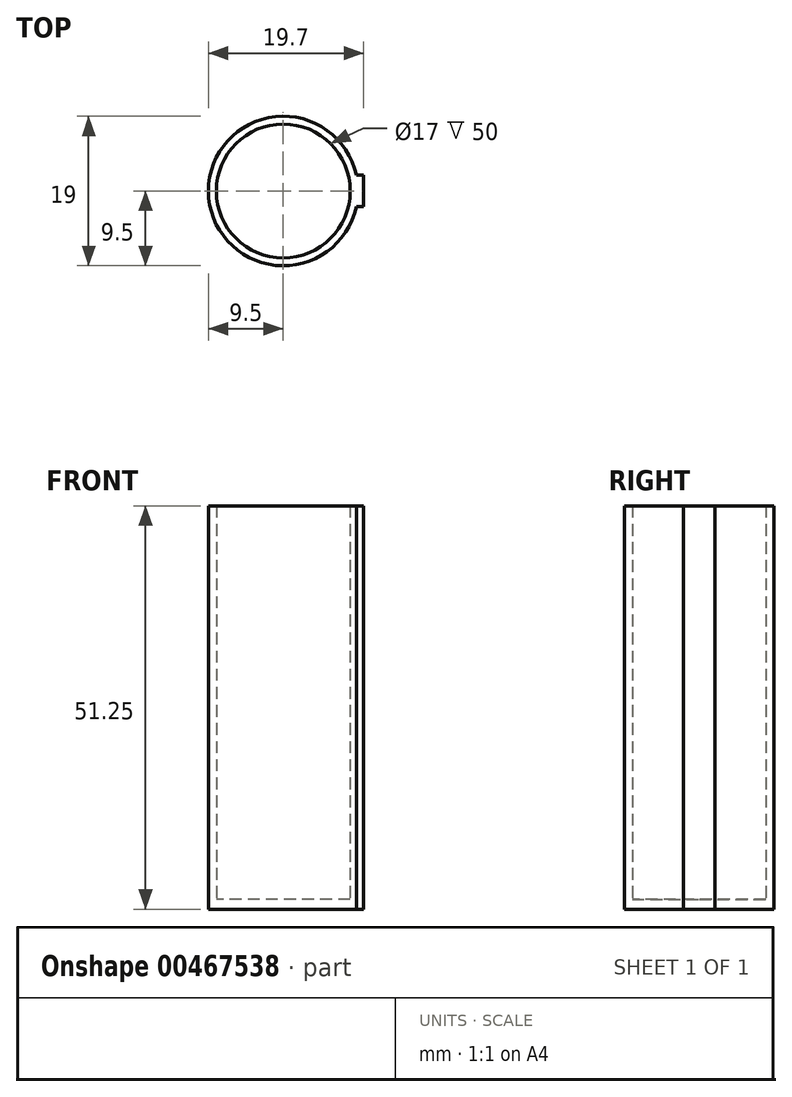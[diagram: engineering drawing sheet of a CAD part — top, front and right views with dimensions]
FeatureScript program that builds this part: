
annotation { "Feature Type Name" : "Feature", "Feature Type Description" : "" }
export const myFeature = defineFeature(function(context is Context, id is Id, definition is map)
    precondition{}
    {
        {
            var Q0;
            Q0=qCreatedBy(makeId("Top.planeOp"),FACE);
            var sketch = newSketch(context, id + "F0", { "sketchPlane" : qUnion([Q0])});
            skCircle(sketch, "E0", {"center": v(0, 0) * mm, "radius": 9.5 * mm});
            skCircle(sketch, "E1", {"center": v(0, 0) * mm, "radius": 8.5 * mm});
            skLineSegment(sketch, "E2.bottom", {"start": v(0, 0) * mm, "end": v(9.5, 0) * mm, "construction": true});
            skLineSegment(sketch, "E2.top", {"start": v(0, 2) * mm, "end": v(9.5, 2) * mm, "construction": true});
            skLineSegment(sketch, "E2.left", {"start": v(0, 0) * mm, "end": v(0, 2) * mm, "construction": true});
            skLineSegment(sketch, "E2.right", {"start": v(9.5, 0) * mm, "end": v(9.5, 2) * mm, "construction": true});
            skLineSegment(sketch, "E3.top", {"start": v(0, -1) * mm, "end": v(9.5, -1) * mm, "construction": true});
            skLineSegment(sketch, "E3.left", {"start": v(0, 0) * mm, "end": v(0, -1) * mm, "construction": true});
            skLineSegment(sketch, "E3.right", {"start": v(9.5, 0) * mm, "end": v(9.5, -1) * mm, "construction": true});
            skLineSegment(sketch, "E4.bottom", {"start": v(10.2, 2) * mm, "end": v(8.8, 2) * mm});
            skLineSegment(sketch, "E4.top", {"start": v(10.2, -2) * mm, "end": v(8.8, -2) * mm});
            skLineSegment(sketch, "E4.left", {"start": v(10.2, 2) * mm, "end": v(10.2, -2) * mm});
            skLineSegment(sketch, "E4.right", {"start": v(8.8, 2) * mm, "end": v(8.8, -2) * mm});
            skPoint(sketch, "E4.middle", {"position": v(9.5, 0) * mm});
            skSolve(sketch);
        }
        {
            var Q0;
            Q0 = qSketchRegion(id + "F0", true);
            extrude(context, id + "F1", {"entities" : qUnion([Q0]), "depth" : 50 * mm, "offsetDistance" : 25 * mm});
        }
        {
            var Q0;
            Q0=makeQuery(id+"F0.imprint","IMPRINT",FACE,{"disambiguationData":[TD([[makeQuery(id+"F0.imprint","IMPRINT",EDGE,{"derivedFrom":sQuery(id+"F0.wireOp",EDGE,"E0")}),1.0]])]});
            var Q1;
            Q1=makeQuery(id+"F0.imprint","IMPRINT",FACE,{"disambiguationData":[TD([[makeQuery(id+"F0.imprint","IMPRINT",EDGE,{"derivedFrom":sQuery(id+"F0.wireOp",EDGE,"E1")}),1.0]])]});
            var Q2;
            Q2=makeQuery(id+"F0.imprint","IMPRINT",FACE,{"disambiguationData":[TD([[makeQuery(id+"F0.imprint","IMPRINT",EDGE,{"derivedFrom":sQuery(id+"F0.wireOp",EDGE,"E1")}),-1.0]])]});
            var Q3;
            {var subQ5=sQuery(id+"F0.wireOp",EDGE,"E4.left");Q3=makeQuery(id+"F0.imprint","IMPRINT",FACE,{"disambiguationData":[TD([[makeQuery(id+"F0.imprint","IMPRINT",EDGE,{"derivedFrom":subQ5}),-1.0]])]});}
            extrude(context, id + "F2", {"entities" : qUnion([Q0, Q1, Q2, Q3]), "operationType" : NewBodyOperationType.ADD, "oppositeDirection" : true, "depth" : 1.25 * mm, "offsetDistance" : 25 * mm});
        }
    });
